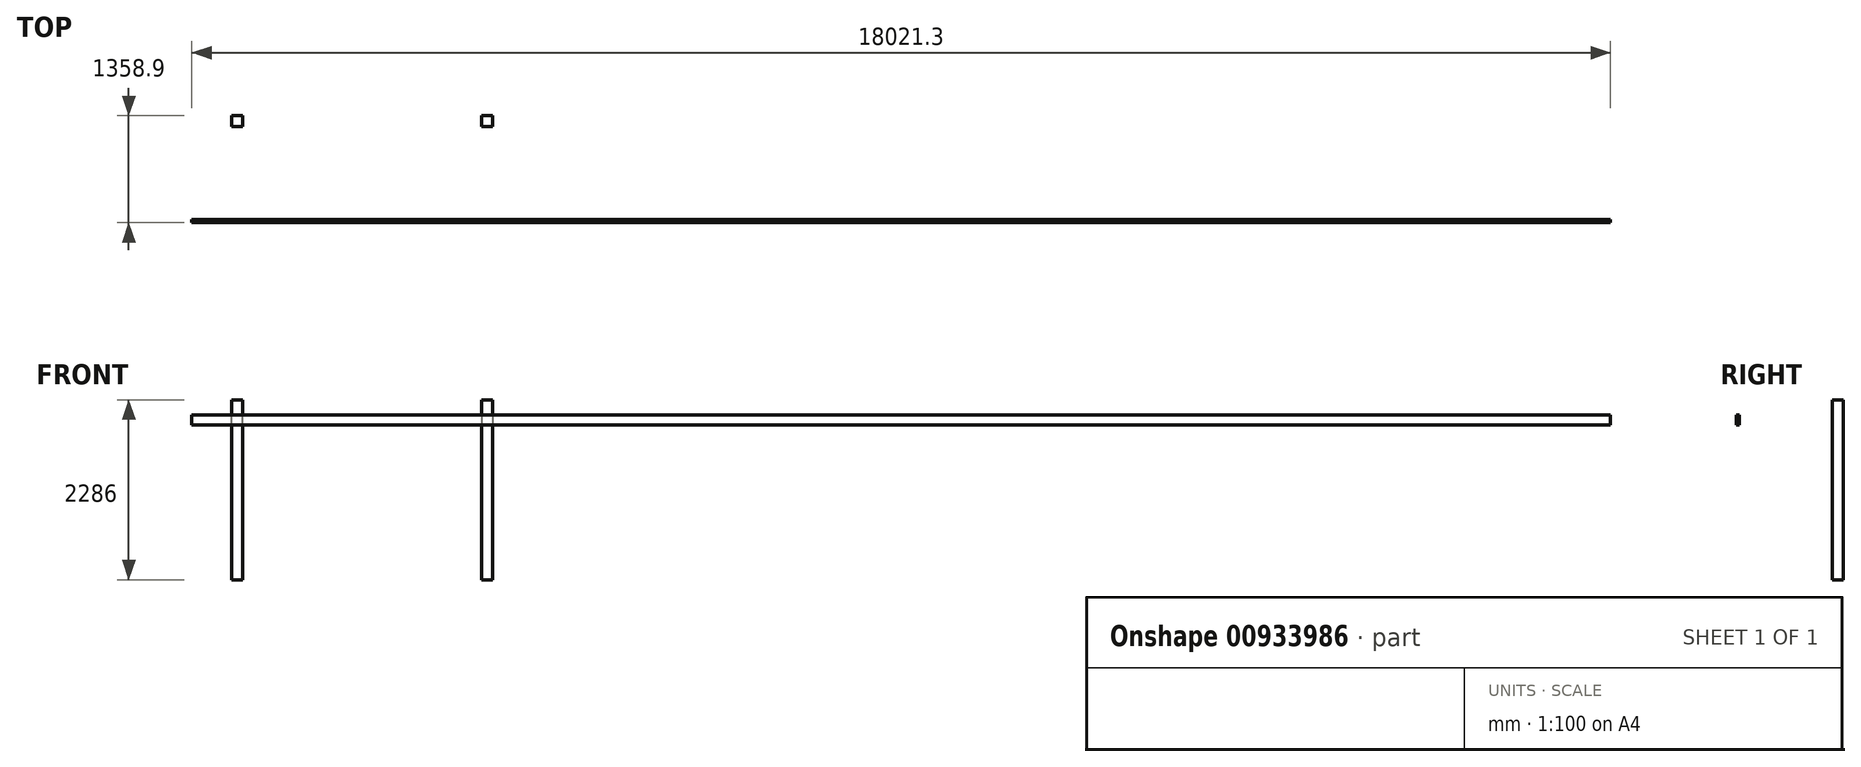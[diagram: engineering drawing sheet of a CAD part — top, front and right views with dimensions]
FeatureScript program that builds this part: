
annotation { "Feature Type Name" : "Feature", "Feature Type Description" : "" }
export const myFeature = defineFeature(function(context is Context, id is Id, definition is map)
    precondition{}
    {
        {
            var Q0;
            Q0=qCreatedBy(makeId("Right.planeOp"),FACE);
            var sketch = newSketch(context, id + "F0", { "sketchPlane" : qUnion([Q0])});
            skLineSegment(sketch, "E0.bottom", {"start": v(-19.05, 63.5) * mm, "end": v(19.05, 63.5) * mm});
            skLineSegment(sketch, "E0.top", {"start": v(-19.05, -63.5) * mm, "end": v(19.05, -63.5) * mm});
            skLineSegment(sketch, "E0.left", {"start": v(-19.05, 63.5) * mm, "end": v(-19.05, -63.5) * mm});
            skLineSegment(sketch, "E0.right", {"start": v(19.05, 63.5) * mm, "end": v(19.05, -63.5) * mm});
            skPoint(sketch, "E0.middle", {"position": v(0, 0) * mm});
            skSolve(sketch);
        }
        {
            var Q0;
            Q0 = qSketchRegion(id + "F0", true);
            extrude(context, id + "F1", {"entities" : qUnion([Q0]), "depth" : 18021.3 * mm, "offsetDistance" : 25.4 * mm});
        }
        {
            var Q0;
            Q0=qCreatedBy(makeId("Top.planeOp"),FACE);
            var sketch = newSketch(context, id + "F2", { "sketchPlane" : qUnion([Q0])});
            skLineSegment(sketch, "E1.bottom", {"start": v(647.7, 1200.15) * mm, "end": v(508, 1200.15) * mm});
            skLineSegment(sketch, "E1.top", {"start": v(647.7, 1339.85) * mm, "end": v(508, 1339.85) * mm});
            skLineSegment(sketch, "E1.left", {"start": v(647.7, 1200.15) * mm, "end": v(647.7, 1339.85) * mm});
            skLineSegment(sketch, "E1.right", {"start": v(508, 1200.15) * mm, "end": v(508, 1339.85) * mm});
            skPoint(sketch, "E1.middle", {"position": v(577.85, 1270) * mm});
            skSolve(sketch);
        }
        {
            var Q0;
            Q0 = qSketchRegion(id + "F2", true);
            extrude(context, id + "F3", {"entities" : qUnion([Q0]), "oppositeDirection" : true, "depth" : 2032 * mm, "offsetDistance" : 25.4 * mm, "hasSecondDirection" : true, "secondDirectionOppositeDirection" : false, "secondDirectionDepth" : 254 * mm});
        }
        {
            var Q0;
            Q0=qCreatedBy(makeId("Top.planeOp"),FACE);
            var sketch = newSketch(context, id + "F4", { "sketchPlane" : qUnion([Q0])});
            skLineSegment(sketch, "E2.bottom", {"start": v(3683, 1200.15) * mm, "end": v(3822.7, 1200.15) * mm});
            skLineSegment(sketch, "E2.top", {"start": v(3683, 1339.85) * mm, "end": v(3822.7, 1339.85) * mm});
            skLineSegment(sketch, "E2.left", {"start": v(3683, 1200.15) * mm, "end": v(3683, 1339.85) * mm});
            skLineSegment(sketch, "E2.right", {"start": v(3822.7, 1200.15) * mm, "end": v(3822.7, 1339.85) * mm});
            skPoint(sketch, "E2.middle", {"position": v(3752.85, 1270) * mm});
            skSolve(sketch);
        }
        {
            var Q0;
            Q0 = qSketchRegion(id + "F4", true);
            extrude(context, id + "F5", {"entities" : qUnion([Q0]), "depth" : 254 * mm, "offsetDistance" : 25.4 * mm, "hasSecondDirection" : true, "secondDirectionOppositeDirection" : true, "secondDirectionDepth" : 2032 * mm});
        }
    });
